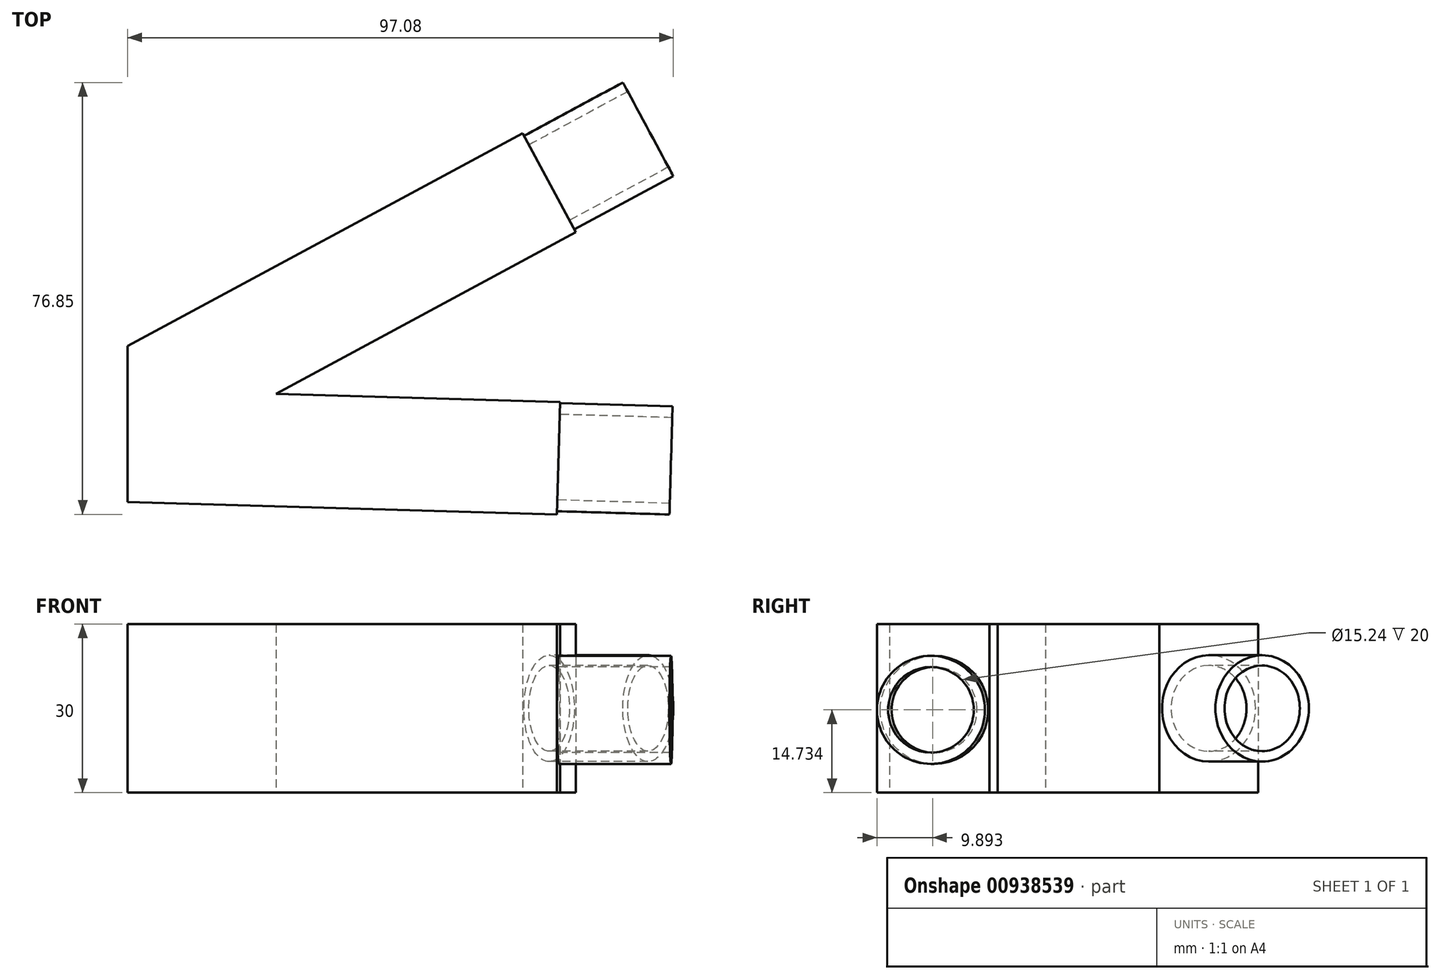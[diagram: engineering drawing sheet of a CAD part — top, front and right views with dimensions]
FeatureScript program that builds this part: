
annotation { "Feature Type Name" : "Feature", "Feature Type Description" : "" }
export const myFeature = defineFeature(function(context is Context, id is Id, definition is map)
    precondition{}
    {
        {
            var Q0;
            Q0=qCreatedBy(makeId("Top.planeOp"),FACE);
            var sketch = newSketch(context, id + "F0", { "sketchPlane" : qUnion([Q0])});
            skLineSegment(sketch, "E0", {"start": v(-57.54, -26.03) * mm, "end": v(-7.57, -27.48) * mm});
            skLineSegment(sketch, "E1", {"start": v(-7.57, -27.48) * mm, "end": v(-6.99, -7.49) * mm});
            skLineSegment(sketch, "E2", {"start": v(-6.99, -7.49) * mm, "end": v(-57.54, -6.02) * mm});
            skLineSegment(sketch, "E3", {"start": v(-57.54, -6.02) * mm, "end": v(-4.21, 22.74) * mm});
            skLineSegment(sketch, "E4", {"start": v(-4.21, 22.74) * mm, "end": v(-13.7, 40.34) * mm});
            skLineSegment(sketch, "E5", {"start": v(-13.7, 40.34) * mm, "end": v(-83.95, 2.46) * mm});
            skLineSegment(sketch, "E6", {"start": v(-57.54, -26.03) * mm, "end": v(-83.95, -25.26) * mm});
            skLineSegment(sketch, "E7", {"start": v(-83.95, 2.46) * mm, "end": v(-83.95, -25.26) * mm});
            skSolve(sketch);
        }
        {
            var Q0;
            Q0 = qSketchRegion(id + "F0", true);
            extrude(context, id + "F1", {"entities" : qUnion([Q0]), "depth" : 15 * mm, "offsetDistance" : 25 * mm});
        }
        {
            var Q0;
            Q0=makeQuery(id+"F1.opExtrude","CAP_FACE",FACE,{"disambiguationData":[OSD([sQuery(id+"F0.wireOp",EDGE,"E0"),sQuery(id+"F0.wireOp",EDGE,"E1"),sQuery(id+"F0.wireOp",EDGE,"E2"),sQuery(id+"F0.wireOp",EDGE,"E3"),sQuery(id+"F0.wireOp",EDGE,"E4"),sQuery(id+"F0.wireOp",EDGE,"E5"),sQuery(id+"F0.wireOp",EDGE,"E6"),sQuery(id+"F0.wireOp",EDGE,"E7")])],"isStart":true});
            extrude(context, id + "F2", {"entities" : qUnion([Q0]), "operationType" : NewBodyOperationType.ADD, "depth" : 15 * mm, "offsetDistance" : 25 * mm});
        }
        {
            var Q0;
            {var subQ0=sQuery(id+"F0.wireOp",EDGE,"E4");Q0=makeQuery(id+"F2.boolean.opBoolean","MERGE",FACE,{"derivedFrom":[makeQuery(id+"F1.opExtrude","SWEPT_FACE",FACE,{"disambiguationData":[OSD([subQ0])]}),makeQuery(id+"F2.opExtrude","SWEPT_FACE",FACE,{"disambiguationData":[OSD([subQ0])]})]});}
            var sketch = newSketch(context, id + "F3", { "sketchPlane" : qUnion([Q0])});
            skLineSegment(sketch, "E8", {"start": v(42.02, 15) * mm, "end": v(22.02, -15) * mm, "construction": true});
            skLineSegment(sketch, "E9", {"start": v(22.02, -15) * mm, "end": v(42.02, -15) * mm, "construction": true});
            skLineSegment(sketch, "E10", {"start": v(42.02, -15) * mm, "end": v(22.02, 15) * mm, "construction": true});
            skCircle(sketch, "E11", {"center": v(32.02, 0) * mm, "radius": 7.62 * mm, "construction": true});
            skCircle(sketch, "E12", {"center": v(32.02, 0) * mm, "radius": 7.62 * mm});
            skCircle(sketch, "E13", {"center": v(32.02, 0) * mm, "radius": 9.46 * mm});
            skSolve(sketch);
        }
        {
            var Q0;
            Q0 = qSketchRegion(id + "F3", true);
            extrude(context, id + "F4", {"entities" : qUnion([Q0]), "operationType" : NewBodyOperationType.ADD, "depth" : 20 * mm, "offsetDistance" : 25 * mm});
        }
        {
            var Q0;
            {var subQ0=sQuery(id+"F0.wireOp",EDGE,"E1");Q0=makeQuery(id+"F2.boolean.opBoolean","MERGE",FACE,{"derivedFrom":[makeQuery(id+"F1.opExtrude","SWEPT_FACE",FACE,{"disambiguationData":[OSD([subQ0])]}),makeQuery(id+"F2.opExtrude","SWEPT_FACE",FACE,{"disambiguationData":[OSD([subQ0])]})]});}
            var sketch = newSketch(context, id + "F5", { "sketchPlane" : qUnion([Q0])});
            skLineSegment(sketch, "E14", {"start": v(-7.69, 15) * mm, "end": v(-27.69, -16.08) * mm, "construction": true});
            skLineSegment(sketch, "E15", {"start": v(-7.69, -15) * mm, "end": v(-27.69, 15) * mm, "construction": true});
            skCircle(sketch, "E16", {"center": v(-17.51, -0.27) * mm, "radius": 7.62 * mm});
            skCircle(sketch, "E17", {"center": v(-17.51, -0.27) * mm, "radius": 9.61 * mm});
            skSolve(sketch);
        }
        {
            var Q0;
            Q0=makeQuery(id+"F5.imprint","IMPRINT",FACE,{"disambiguationData":[TD([[makeQuery(id+"F5.imprint","IMPRINT",EDGE,{"derivedFrom":sQuery(id+"F5.wireOp",EDGE,"E16")}),-1.0]])]});
            extrude(context, id + "F6", {"entities" : qUnion([Q0]), "operationType" : NewBodyOperationType.ADD, "depth" : 20 * mm, "offsetDistance" : 25 * mm});
        }
    });
